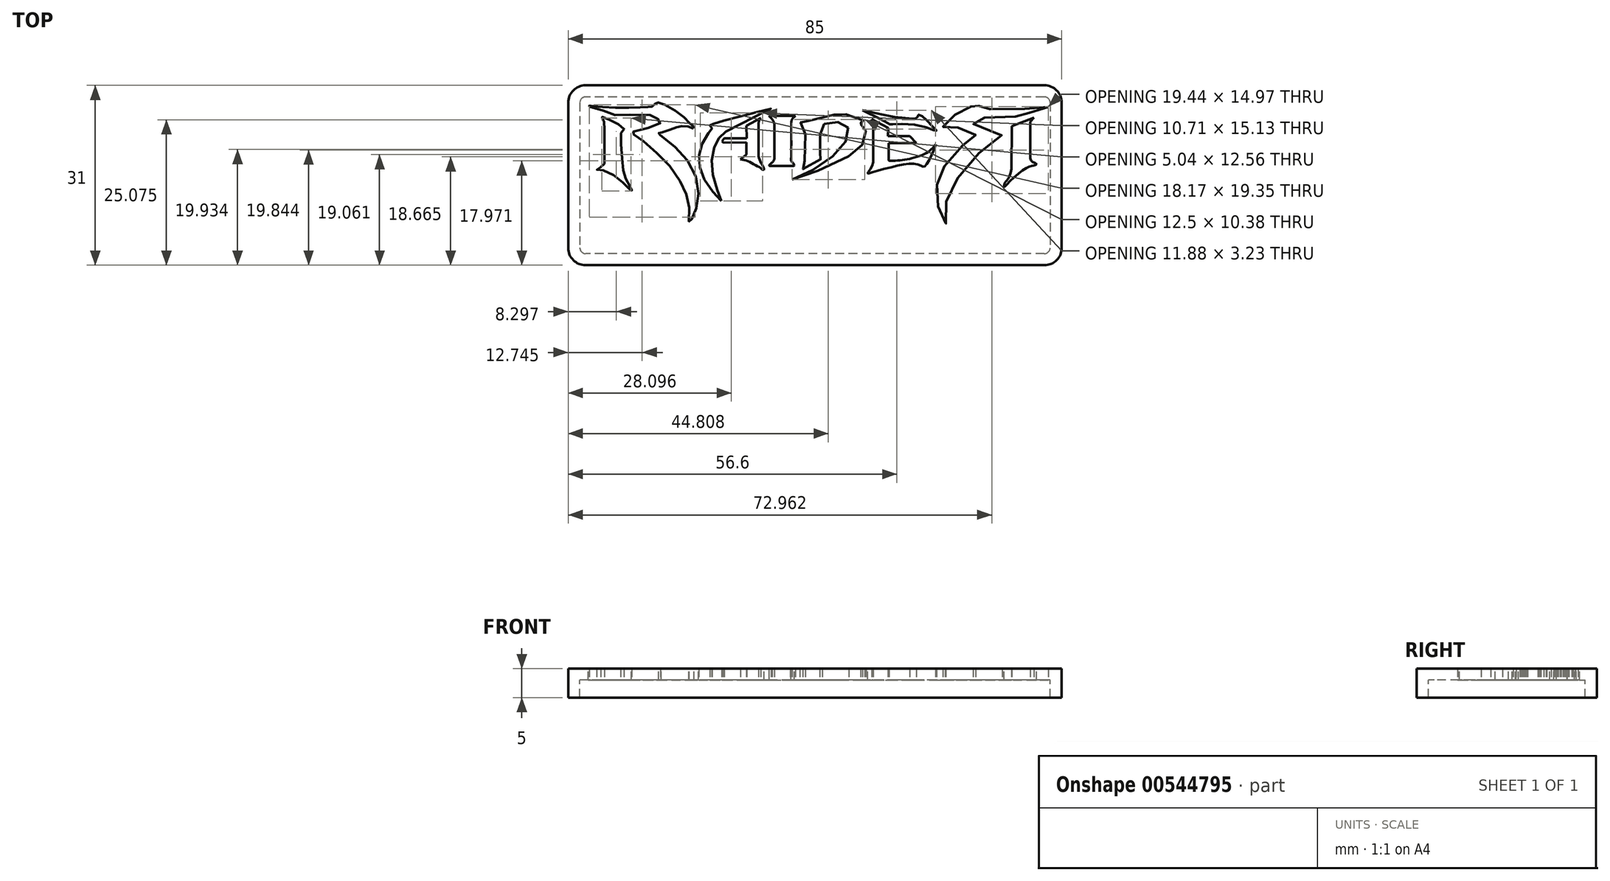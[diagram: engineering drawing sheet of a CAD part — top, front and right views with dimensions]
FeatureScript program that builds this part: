
annotation { "Feature Type Name" : "Feature", "Feature Type Description" : "" }
export const myFeature = defineFeature(function(context is Context, id is Id, definition is map)
    precondition{}
    {
        {
            var Q0;
            Q0=qCreatedBy(makeId("Top.planeOp"),FACE);
            var sketch = newSketch(context, id + "F0", { "sketchPlane" : qUnion([Q0])});
            skFitSpline(sketch, "E0", {"points": [v(-36.64, 6.62) * mm, v(-36.43, 6.32) * mm, v(-36.28, 5.66) * mm, v(-36.26, 2.74) * mm, v(-36.24, -1.06) * mm, v(-36.3, -1.25) * mm, v(-37, -1.91) * mm, v(-37.58, -2.19) * mm, v(-37.53, -2.26) * mm, v(-36.5, -2.37) * mm, v(-33.52, -4.06) * mm, v(-31.97, -5.62) * mm, v(-31.6, -5.96) * mm, v(-31.6, -5.55) * mm, v(-31.89, -5.13) * mm, v(-32.74, -3.53) * mm, v(-33.13, -1.15) * mm, v(-33.45, 3.54) * mm, v(-33.08, 4.6) * mm, v(-32.87, 4.8) * mm, v(-34.93, 6.12) * mm, v(-36.33, 6.76) * mm, v(-36.89, 6.9) * mm, v(-36.64, 6.62) * mm]});
            skFitSpline(sketch, "E1", {"points": [v(-38.84, 8.62) * mm, v(-36.38, 7.9) * mm, v(-34.46, 7.19) * mm, v(-33.92, 7.16) * mm, v(-28.5, 7.15) * mm, v(-28.13, 7.05) * mm, v(-27.13, 6.5) * mm, v(-26.52, 5.97) * mm, v(-26.51, 5.88) * mm, v(-26.87, 5.6) * mm, v(-29.6, 4.71) * mm, v(-31.53, 4.2) * mm, v(-31.63, 4.12) * mm, v(-31.33, 3.83) * mm, v(-30.77, 3.62) * mm, v(-28.58, 1.85) * mm, v(-25.7, -0.88) * mm, v(-23.28, -4.13) * mm, v(-22.17, -6.58) * mm, v(-21.65, -8.78) * mm, v(-21.7, -11.17) * mm, v(-21.62, -11.37) * mm, v(-21.4, -11.09) * mm, v(-21.09, -10.5) * mm, v(-20.43, -8.76) * mm, v(-20.06, -6.03) * mm, v(-21, -2.3) * mm, v(-23.42, 1.06) * mm, v(-26.58, 3.67) * mm], "startDerivative": vector(50.9, -13.14) * mm, "endDerivative": vector(-57.94, 43.06) * mm});
            skFitSpline(sketch, "E2", {"points": [v(-26.58, 3.67) * mm, v(-26.96, 3.96) * mm, v(-26.77, 4.14) * mm, v(-26.4, 4.16) * mm, v(-24.33, 4.87) * mm, v(-23.27, 5.19) * mm, v(-22.07, 5.25) * mm, v(-21.14, 4.89) * mm, v(-20.86, 4.88) * mm, v(-20.9, 5.12) * mm, v(-21.48, 5.7) * mm, v(-23.48, 7.5) * mm, v(-26.77, 9.28) * mm, v(-27.14, 9.3) * mm, v(-27.48, 9.12) * mm, v(-27.98, 8.68) * mm, v(-28.47, 8.55) * mm, v(-30.01, 8.47) * mm, v(-35.35, 8.48) * mm, v(-38.4, 8.71) * mm, v(-38.71, 8.75) * mm, v(-39.04, 8.74) * mm, v(-38.84, 8.62) * mm], "startDerivative": vector(-17.53, 8.78) * mm, "endDerivative": vector(7.39, -3.14) * mm});
            skFitSpline(sketch, "E3", {"points": [v(-16.1, -7.62) * mm, v(-18.04, -5.46) * mm, v(-19.5, -3.01) * mm, v(-19.99, -0.3) * mm, v(-19.6, 1.72) * mm, v(-18.5, 3.85) * mm, v(-17.84, 4.63) * mm, v(-17.73, 4.84) * mm, v(-17.8, 5.17) * mm, v(-17.98, 5.3) * mm, v(-18.08, 5.4) * mm, v(-17.99, 5.6) * mm, v(-17.74, 5.6) * mm, v(-17.38, 5.72) * mm, v(-14.14, 6.57) * mm, v(-9.34, 7.82) * mm, v(-7.58, 8.22) * mm, v(-8.24, 7.9) * mm, v(-9.45, 7.31) * mm, v(-13.57, 5.26) * mm, v(-16.02, 3.83) * mm, v(-16.6, 3.02) * mm, v(-17.45, 1.23) * mm, v(-17.79, -1.8) * mm, v(-16.95, -5.4) * mm, v(-16.1, -7.62) * mm]});
            skLineSegment(sketch, "E4", {"start": v(-15.65, 3.16) * mm, "end": v(-11.76, 3.16) * mm});
            skLineSegment(sketch, "E5", {"start": v(-11.76, 3.16) * mm, "end": v(-11.8, 5.3) * mm});
            skLineSegment(sketch, "E6", {"start": v(-11.8, 5.3) * mm, "end": v(-9.35, 6.62) * mm});
            skLineSegment(sketch, "E7", {"start": v(-15.65, 3.16) * mm, "end": v(-16, 2.65) * mm});
            skLineSegment(sketch, "E8", {"start": v(-16, 2.65) * mm, "end": v(-15.74, 2.38) * mm});
            skLineSegment(sketch, "E9", {"start": v(-15.74, 2.38) * mm, "end": v(-11.85, 2.44) * mm});
            skLineSegment(sketch, "E10", {"start": v(-11.85, 2.44) * mm, "end": v(-11.8, 0.34) * mm});
            skLineSegment(sketch, "E11", {"start": v(-11.8, 0.34) * mm, "end": v(-12.86, -0.48) * mm});
            skLineSegment(sketch, "E12", {"start": v(-9.74, 5.38) * mm, "end": v(-9.74, 0.13) * mm});
            skLineSegment(sketch, "E13", {"start": v(-6.96, 5.4) * mm, "end": v(-6.96, -0.12) * mm});
            skLineSegment(sketch, "E14", {"start": v(-7.97, 7) * mm, "end": v(-3.38, 7) * mm});
            skLineSegment(sketch, "E15", {"start": v(-4.1, 5.5) * mm, "end": v(-4.1, -0.15) * mm});
            skLineSegment(sketch, "E16", {"start": v(-7.35, -1.6) * mm, "end": v(-4.24, -1.6) * mm});
            skFitSpline(sketch, "E17", {"points": [v(-9.35, 6.62) * mm, v(-9.74, 5.38) * mm], "startDerivative": vector(-1.04, -1.04) * mm, "endDerivative": vector(-0.12, -1.58) * mm});
            skFitSpline(sketch, "E18", {"points": [v(-9.74, 0.13) * mm, v(-9.37, -0.98) * mm, v(-8.86, -1.87) * mm, v(-8.81, -2.27) * mm, v(-9.03, -2.26) * mm, v(-9.43, -1.94) * mm, v(-10.64, -1.27) * mm, v(-11.82, -0.7) * mm, v(-12.86, -0.48) * mm], "startDerivative": vector(1.77, -7.95) * mm, "endDerivative": vector(-7.6, 1.12) * mm});
            skFitSpline(sketch, "E19", {"points": [v(-7.97, 7) * mm, v(-7.21, 6.2) * mm, v(-6.96, 5.4) * mm], "startDerivative": vector(1.66, -1.43) * mm, "endDerivative": vector(0.34, -1.77) * mm});
            skFitSpline(sketch, "E20", {"points": [v(-3.38, 7) * mm, v(-3.97, 6.38) * mm, v(-4.1, 5.5) * mm], "startDerivative": vector(-1.43, -1.11) * mm, "endDerivative": vector(-0.02, -1.86) * mm});
            skFitSpline(sketch, "E21", {"points": [v(-6.96, -0.12) * mm, v(-7.2, -0.85) * mm, v(-7.86, -1.46) * mm, v(-7.85, -1.58) * mm, v(-7.35, -1.6) * mm], "startDerivative": vector(-0.27, -2.47) * mm, "endDerivative": vector(2.58, 0.33) * mm});
            skFitSpline(sketch, "E22", {"points": [v(-4.1, -0.15) * mm, v(-4.1, -0.74) * mm, v(-3.7, -1.21) * mm, v(-3.6, -1.6) * mm, v(-3.8, -1.6) * mm, v(-4.24, -1.6) * mm], "startDerivative": vector(-0.48, -2.72) * mm, "endDerivative": vector(-2.35, -0.14) * mm});
            skFitSpline(sketch, "E23", {"points": [v(-3.94, -3.98) * mm, v(0.45, -1.84) * mm, v(3.6, 0.6) * mm, v(5.54, 3.06) * mm, v(5.75, 4.8) * mm, v(5.23, 5.58) * mm, v(3.8, 5.93) * mm, v(2.15, 5.84) * mm, v(1.08, 5.21) * mm, v(0.89, 4.16) * mm, v(0.85, 0.9) * mm, v(1, 0.38) * mm, v(1.23, -0.1) * mm, v(1.07, -0.4) * mm, v(-1.98, -2.12) * mm, v(-2.09, -2.12) * mm, v(-2, -1.63) * mm, v(-1.77, -0.8) * mm, v(-1.72, 4.8) * mm, v(-2.1, 5.75) * mm, v(-2.63, 5.96) * mm, v(-2.45, 6.08) * mm, v(-0.9, 6.17) * mm, v(4.23, 7.43) * mm, v(4.58, 7.43) * mm, v(6.52, 7.01) * mm, v(8.52, 6.07) * mm, v(8.53, 5.93) * mm, v(7.92, 5.82) * mm, v(7.92, 5.58) * mm, v(8.22, 5.16) * mm, v(8.7, 4.56) * mm, v(8.66, 2.92) * mm, v(7.36, 1.24) * mm, v(3.88, -1.02) * mm, v(-3.94, -3.98) * mm]});
            skFitSpline(sketch, "E24", {"points": [v(8.16, 7.97) * mm, v(10.71, 6.73) * mm, v(12.97, 5.54) * mm, v(13.13, 5.54) * mm, v(18.04, 5.34) * mm, v(20.87, 4.42) * mm, v(20.92, 4.44) * mm, v(19.47, 6) * mm, v(18.2, 7.13) * mm, v(17.78, 7.19) * mm, v(17.68, 6.9) * mm, v(17.43, 6.58) * mm, v(15.76, 6.62) * mm, v(12.87, 6.95) * mm, v(8.62, 7.93) * mm, v(8.16, 7.97) * mm]});
            skFitSpline(sketch, "E25", {"points": [v(20.82, 2.16) * mm, v(19.34, 0.72) * mm, v(15.79, -0.5) * mm, v(12.75, -0.73) * mm], "startDerivative": vector(-4.3, -5.4) * mm, "endDerivative": vector(-8.49, -0.18) * mm});
            skFitSpline(sketch, "E26", {"points": [v(20.82, 2.16) * mm, v(20.1, 0.26) * mm, v(18.88, -1.7) * mm, v(18.52, -1.68) * mm, v(17.36, -1.27) * mm, v(13.54, -1.72) * mm, v(9.37, -2.86) * mm, v(9.1, -2.9) * mm, v(9.29, -2.46) * mm, v(10.04, -0.96) * mm], "startDerivative": vector(-4.6, -13.65) * mm, "endDerivative": vector(2.94, 17.52) * mm});
            skLineSegment(sketch, "E27", {"start": v(10.04, -0.96) * mm, "end": v(10.04, 5.62) * mm});
            skLineSegment(sketch, "E28", {"start": v(10.04, 5.62) * mm, "end": v(9.8, 6.44) * mm});
            skLineSegment(sketch, "E29", {"start": v(9.8, 6.44) * mm, "end": v(12.6, 4.9) * mm});
            skLineSegment(sketch, "E30", {"start": v(12.6, 4.9) * mm, "end": v(12.6, 3.56) * mm});
            skLineSegment(sketch, "E31", {"start": v(12.6, 3.56) * mm, "end": v(16.32, 3.52) * mm});
            skLineSegment(sketch, "E32", {"start": v(16.32, 3.52) * mm, "end": v(17.46, 2.35) * mm});
            skLineSegment(sketch, "E33", {"start": v(17.46, 2.35) * mm, "end": v(12.68, 2.33) * mm});
            skLineSegment(sketch, "E34", {"start": v(12.68, 2.33) * mm, "end": v(12.68, -0.65) * mm});
            skLineSegment(sketch, "E35", {"start": v(12.68, -0.65) * mm, "end": v(12.75, -0.73) * mm});
            skFitSpline(sketch, "E36", {"points": [v(40.18, 8.55) * mm, v(37.12, 8.28) * mm, v(29.53, 8.24) * mm, v(28.87, 8.45) * mm, v(28.22, 8.71) * mm, v(28.04, 9.04) * mm, v(27.81, 9.04) * mm, v(26.77, 8.58) * mm, v(24.72, 7.57) * mm, v(22.86, 6.14) * mm, v(22.04, 5.08) * mm, v(22.11, 5.06) * mm, v(24.29, 5.08) * mm, v(27.54, 3.83) * mm, v(27.68, 3.71) * mm, v(27.52, 3.57) * mm, v(24.83, 1.4) * mm, v(21.84, -2.45) * mm, v(21, -4.85) * mm, v(20.87, -7.46) * mm, v(22.5, -11.68) * mm, v(22.55, -11.65) * mm, v(22.42, -9.1) * mm, v(23.73, -5.06) * mm, v(28.16, 0.5) * mm, v(32.24, 3.77) * mm, v(32.24, 3.88) * mm, v(31.05, 4.25) * mm, v(27.35, 5.4) * mm, v(27.25, 5.56) * mm, v(28.27, 6.43) * mm, v(28.97, 6.7) * mm, v(34.88, 6.92) * mm, v(35.44, 6.97) * mm, v(37.98, 7.89) * mm, v(40.18, 8.55) * mm]});
            skLineSegment(sketch, "E37", {"start": v(37.71, 6.73) * mm, "end": v(33.9, 5.25) * mm});
            skLineSegment(sketch, "E38", {"start": v(33.9, 5.25) * mm, "end": v(33.84, -2.15) * mm});
            skLineSegment(sketch, "E39", {"start": v(37.06, 5.98) * mm, "end": v(37.08, -0.27) * mm});
            skFitSpline(sketch, "E40", {"points": [v(37.08, -0.27) * mm, v(37.42, -0.9) * mm, v(38.1, -1.23) * mm, v(38.11, -1.37) * mm, v(37.7, -1.56) * mm, v(37, -1.72) * mm, v(34.97, -2.98) * mm, v(32.74, -5.14) * mm, v(32.63, -5.2) * mm, v(32.57, -5.09) * mm, v(32.64, -4.67) * mm, v(33.33, -3.69) * mm, v(33.84, -2.15) * mm], "startDerivative": vector(2.58, -8.91) * mm, "endDerivative": vector(3.2, 13.65) * mm});
            skLineSegment(sketch, "E41", {"start": v(37.71, 6.73) * mm, "end": v(37.06, 5.98) * mm});
            skSolve(sketch);
        }
        {
            var Q0;
            Q0=qCreatedBy(makeId("Top.planeOp"),FACE);
            var sketch = newSketch(context, id + "F1", { "sketchPlane" : qUnion([Q0])});
            skLineSegment(sketch, "E42.bottom", {"start": v(42.5, 12.28) * mm, "end": v(-42.5, 12.28) * mm});
            skLineSegment(sketch, "E42.top", {"start": v(42.5, -18.72) * mm, "end": v(-42.5, -18.72) * mm});
            skLineSegment(sketch, "E42.left", {"start": v(42.5, 12.28) * mm, "end": v(42.5, -18.72) * mm});
            skLineSegment(sketch, "E42.right", {"start": v(-42.5, 12.28) * mm, "end": v(-42.5, -18.72) * mm});
            skPoint(sketch, "E42.middle", {"position": v(0, 0) * mm});
            skLineSegment(sketch, "E43", {"start": v(0, 12.28) * mm, "end": v(0, -18.72) * mm, "construction": true});
            skSolve(sketch);
        }
        {
            var Q0;
            Q0=makeQuery(id+"F1.imprint","IMPRINT",FACE,{"disambiguationData":[TD([[makeQuery(id+"F1.imprint","IMPRINT",EDGE,{"derivedFrom":sQuery(id+"F1.wireOp",EDGE,"E42.bottom")}),1.0]])]});
            extrude(context, id + "F2", {"entities" : qUnion([Q0]), "depth" : 2 * mm, "offsetDistance" : 25 * mm});
        }
        {
            var Q0;
            Q0=makeQuery(id+"F2.opExtrude","SWEPT_EDGE",EDGE,{"disambiguationData":[OSD([sQuery(id+"F1.wireOp",EDGE,"E42.top"),sQuery(id+"F1.wireOp",EDGE,"E42.right")])]});
            var Q1;
            Q1=makeQuery(id+"F2.opExtrude","SWEPT_EDGE",EDGE,{"disambiguationData":[OSD([sQuery(id+"F1.wireOp",EDGE,"E42.bottom"),sQuery(id+"F1.wireOp",EDGE,"E42.right")])]});
            var Q2;
            Q2=makeQuery(id+"F2.opExtrude","SWEPT_EDGE",EDGE,{"disambiguationData":[OSD([sQuery(id+"F1.wireOp",EDGE,"E42.top"),sQuery(id+"F1.wireOp",EDGE,"E42.left")])]});
            var Q3;
            Q3=makeQuery(id+"F2.opExtrude","SWEPT_EDGE",EDGE,{"disambiguationData":[OSD([sQuery(id+"F1.wireOp",EDGE,"E42.bottom"),sQuery(id+"F1.wireOp",EDGE,"E42.left")])]});
            fillet(context, id + "F3", {"entities" : qUnion([Q0, Q1, Q2, Q3]), "radius" : 3 * mm, "tangentPropagation" : true, "allowEdgeOverflow" : false});
        }
        {
            var Q0;
            Q0 = qSketchRegion(id + "F0", true);
            extrude(context, id + "F4", {"entities" : qUnion([Q0]), "operationType" : NewBodyOperationType.REMOVE, "endBound" : BoundingType.THROUGH_ALL, "depth" : 25 * mm, "offsetDistance" : 25 * mm});
        }
        {
            var Q0;
            Q0=makeQuery(id+"F2.opExtrude","CAP_FACE",FACE,{"disambiguationData":[OSD([sQuery(id+"F1.wireOp",EDGE,"E42.bottom"),sQuery(id+"F1.wireOp",EDGE,"E42.top"),sQuery(id+"F1.wireOp",EDGE,"E42.left"),sQuery(id+"F1.wireOp",EDGE,"E42.right")])],"isStart":true});
            var sketch = newSketch(context, id + "F5", { "sketchPlane" : qUnion([Q0])});
            skArc(sketch, "E44.0", {"start": v(40.5, 15.72) * mm, "mid": v(40.2, 16.43) * mm, "end": v(39.5, 16.72) * mm});
            skLineSegment(sketch, "E44.1", {"start": v(40.5, -9.28) * mm, "end": v(40.5, 15.72) * mm});
            skLineSegment(sketch, "E44.2", {"start": v(39.5, 16.72) * mm, "end": v(-39.5, 16.72) * mm});
            skArc(sketch, "E44.3", {"start": v(39.5, -10.28) * mm, "mid": v(40.2, -9.98) * mm, "end": v(40.5, -9.28) * mm});
            skArc(sketch, "E44.4", {"start": v(-39.5, 16.72) * mm, "mid": v(-40.2, 16.43) * mm, "end": v(-40.5, 15.72) * mm});
            skLineSegment(sketch, "E44.5", {"start": v(-40.5, -9.28) * mm, "end": v(-40.5, 15.72) * mm});
            skArc(sketch, "E44.6", {"start": v(-40.5, -9.28) * mm, "mid": v(-40.2, -9.98) * mm, "end": v(-39.5, -10.28) * mm});
            skLineSegment(sketch, "E44.7", {"start": v(39.5, -10.28) * mm, "end": v(-39.5, -10.28) * mm});
            skSolve(sketch);
        }
        {
            var Q0;
            Q0=makeQuery(id+"F5.imprint","IMPRINT",FACE,{"disambiguationData":[TD([[makeQuery(id+"F5.imprint","IMPRINT",EDGE,{"derivedFrom":sQuery(id+"F5.wireOp",EDGE,"E44.0")}),-1.0]])]});
            extrude(context, id + "F6", {"entities" : qUnion([Q0]), "operationType" : NewBodyOperationType.ADD, "depth" : 3 * mm, "offsetDistance" : 25 * mm});
        }
    });
